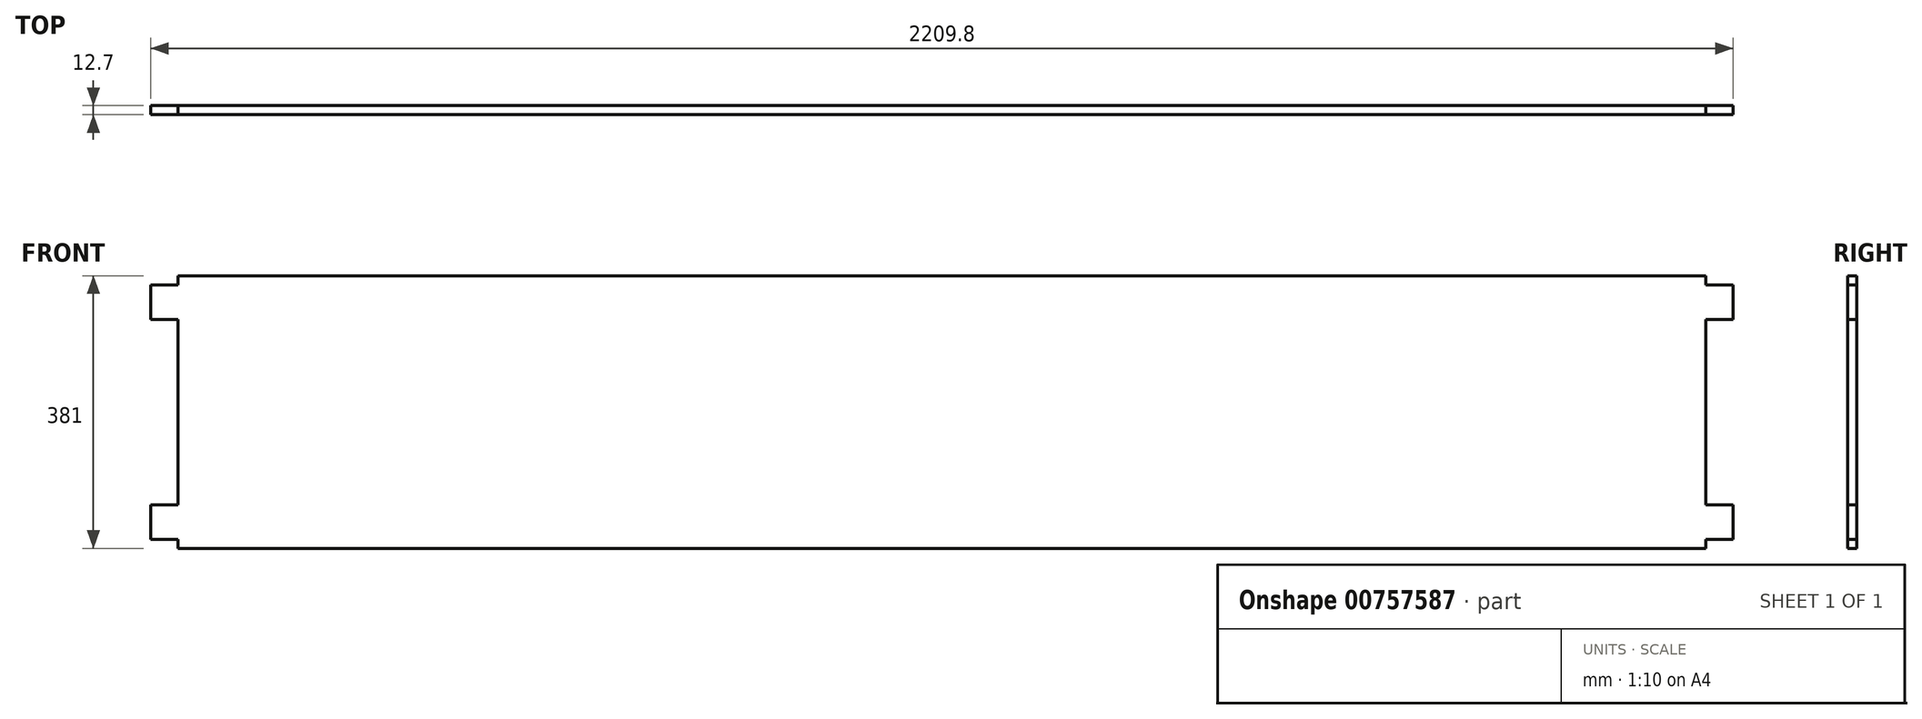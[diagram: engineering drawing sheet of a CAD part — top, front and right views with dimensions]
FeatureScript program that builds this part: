
annotation { "Feature Type Name" : "Feature", "Feature Type Description" : "" }
export const myFeature = defineFeature(function(context is Context, id is Id, definition is map)
    precondition{}
    {
        {
            var Q0;
            Q0=qCreatedBy(makeId("Front.planeOp"),FACE);
            var sketch = newSketch(context, id + "F0", { "sketchPlane" : qUnion([Q0])});
            skLineSegment(sketch, "E0.bottom", {"start": v(-1066.8, 190.5) * mm, "end": v(0, 190.5) * mm});
            skLineSegment(sketch, "E0.left", {"start": v(-1066.8, 190.5) * mm, "end": v(-1066.8, 177.8) * mm});
            skPoint(sketch, "E0.middle", {"position": v(0, 0) * mm});
            skLineSegment(sketch, "E1", {"start": v(-1066.8, 177.8) * mm, "end": v(-1104.9, 177.8) * mm});
            skLineSegment(sketch, "E2", {"start": v(-1104.9, 177.8) * mm, "end": v(-1104.9, 129.54) * mm});
            skLineSegment(sketch, "E3", {"start": v(-1104.9, 129.54) * mm, "end": v(-1066.8, 129.54) * mm});
            skLineSegment(sketch, "E4", {"start": v(-1066.8, 0) * mm, "end": v(1066.8, 0) * mm, "construction": true});
            skLineSegment(sketch, "E5", {"start": v(0, 190.5) * mm, "end": v(0, -190.5) * mm, "construction": true});
            skLineSegment(sketch, "E6.trimOffspring", {"start": v(-1066.8, 129.54) * mm, "end": v(-1066.8, 0) * mm});
            skLineSegment(sketch, "E7.MirrorCS", {"start": v(-1066.8, -190.5) * mm, "end": v(-1066.8, -177.8) * mm});
            skLineSegment(sketch, "E8.MirrorCS", {"start": v(-1066.8, -177.8) * mm, "end": v(-1104.9, -177.8) * mm});
            skLineSegment(sketch, "E9.MirrorCS", {"start": v(-1066.8, -190.5) * mm, "end": v(0, -190.5) * mm});
            skLineSegment(sketch, "E10.MirrorCS", {"start": v(-1104.9, -177.8) * mm, "end": v(-1104.9, -129.54) * mm});
            skLineSegment(sketch, "E11.MirrorCS", {"start": v(-1066.8, -129.54) * mm, "end": v(-1066.8, 0) * mm});
            skLineSegment(sketch, "E12.MirrorCS", {"start": v(-1104.9, -129.54) * mm, "end": v(-1066.8, -129.54) * mm});
            skLineSegment(sketch, "E13.MirrorCS", {"start": v(1066.8, 190.5) * mm, "end": v(0, 190.5) * mm});
            skLineSegment(sketch, "E14.MirrorCS", {"start": v(1066.8, -190.5) * mm, "end": v(0, -190.5) * mm});
            skLineSegment(sketch, "E15.MirrorCS", {"start": v(1066.8, -190.5) * mm, "end": v(1066.8, -177.8) * mm});
            skLineSegment(sketch, "E16.MirrorCS", {"start": v(1066.8, 190.5) * mm, "end": v(1066.8, 177.8) * mm});
            skLineSegment(sketch, "E17.MirrorCS", {"start": v(1104.9, -129.54) * mm, "end": v(1066.8, -129.54) * mm});
            skLineSegment(sketch, "E18.MirrorCS", {"start": v(1066.8, -129.54) * mm, "end": v(1066.8, 0) * mm});
            skLineSegment(sketch, "E19.MirrorCS", {"start": v(1066.8, -177.8) * mm, "end": v(1104.9, -177.8) * mm});
            skLineSegment(sketch, "E20.MirrorCS", {"start": v(1104.9, -177.8) * mm, "end": v(1104.9, -129.54) * mm});
            skLineSegment(sketch, "E21.MirrorCS", {"start": v(1066.8, 177.8) * mm, "end": v(1104.9, 177.8) * mm});
            skLineSegment(sketch, "E22.MirrorCS", {"start": v(1066.8, 129.54) * mm, "end": v(1066.8, 0) * mm});
            skLineSegment(sketch, "E23.MirrorCS", {"start": v(1104.9, 177.8) * mm, "end": v(1104.9, 129.54) * mm});
            skLineSegment(sketch, "E24.MirrorCS", {"start": v(1104.9, 129.54) * mm, "end": v(1066.8, 129.54) * mm});
            skSolve(sketch);
        }
        {
            var Q0;
            Q0 = qSketchRegion(id + "F0", true);
            extrude(context, id + "F1", {"entities" : qUnion([Q0]), "endBound" : BoundingType.SYMMETRIC, "depth" : 12.7 * mm, "offsetDistance" : 25.4 * mm});
        }
    });
